# Revit family: Unit_Compact-Teknion-Zones_ZNRC-R2015
name_source: partatom
category: Furniture
revit_build: Autodesk Revit 2015 (Build: 20140223_1515(x64)
units: mm (PartAtom-declared; Revit-internal decimal feet)

## types (4) — shared parameters
Assembly Code = E2020200
Depth = 16"
Height = 42"
Manufacturer = Teknion
Manufacturer Fax = 416.661.4586
Part Number = ZNRC
Product Documentation Link = http://www.teknion.com
Product Line = Zones
Product Page URL = http://www.teknion.com
Series = Zones
Sustainability Data = http://www.teknion.com
URL = http://www.teknion.com
Warranty = http://www.teknion.com
Width = 16"

## per-type parameters (varying)
| type | Description | Model | With Casters | With Cubby Tray | With Levellers |
| Unit | Compact Mobile Unit, 42"h x 16"w, No Casters, No Cubby Trays | ZNRC4216NN | No | No | Yes |
| Unit with Cubby Tray | Compact Mobile Unit, 42"h x 16"w, No Casters, Cubby Trays | ZNRC4216NY | No | Yes | Yes |
| Unit with Casters | Compact Mobile Unit, 42"h x 16"w, Casters, No Cubby Trays | ZNRC4216YN | Yes | No | No |
| Unit with Casters and Cubby Tray | Compact Mobile Unit, 42"h x 16"w, Casters, Cubby Trays | ZNRC4216YY | Yes | Yes | No |

## geometry (parser evidence)
native form markers: Blend x6, Sweep x10
no freeform markers — native parametric forms only
